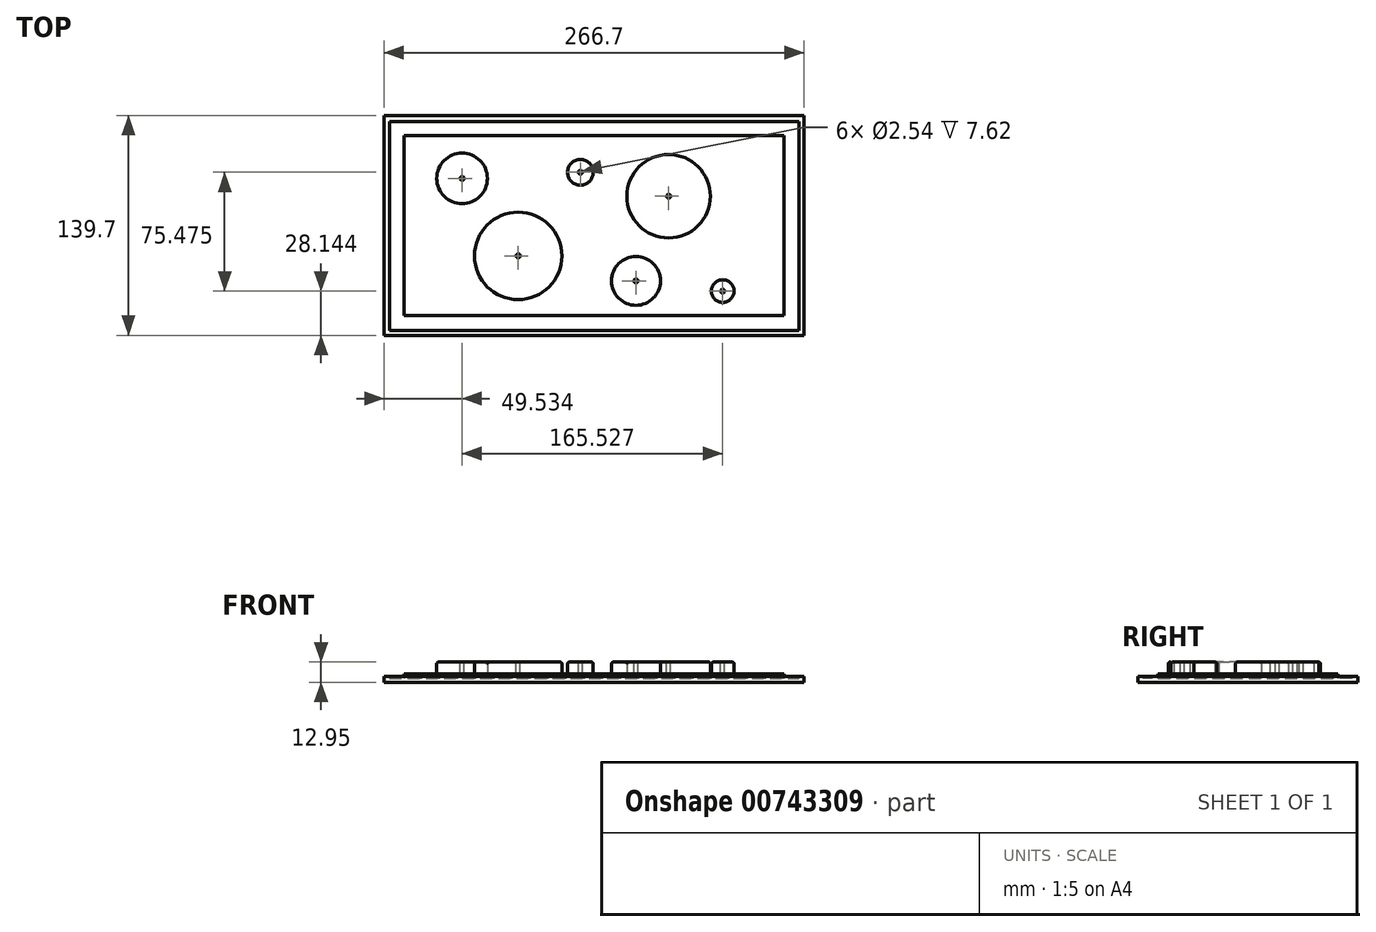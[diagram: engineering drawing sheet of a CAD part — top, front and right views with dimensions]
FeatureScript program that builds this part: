
annotation { "Feature Type Name" : "Feature", "Feature Type Description" : "" }
export const myFeature = defineFeature(function(context is Context, id is Id, definition is map)
    precondition{}
    {
        {
            var Q0;
            Q0=qCreatedBy(makeId("Top.planeOp"),FACE);
            var sketch = newSketch(context, id + "F0", { "sketchPlane" : qUnion([Q0])});
            skLineSegment(sketch, "E0.bottom", {"start": v(-127, 63.5) * mm, "end": v(127, 63.5) * mm});
            skLineSegment(sketch, "E0.top", {"start": v(-127, -63.5) * mm, "end": v(127, -63.5) * mm});
            skLineSegment(sketch, "E0.left", {"start": v(-127, 63.5) * mm, "end": v(-127, -63.5) * mm});
            skLineSegment(sketch, "E0.right", {"start": v(127, 63.5) * mm, "end": v(127, -63.5) * mm});
            skPoint(sketch, "E0.middle", {"position": v(0, 0) * mm});
            skSolve(sketch);
        }
        {
            var Q0;
            Q0 = qSketchRegion(id + "F0", true);
            extrude(context, id + "F1", {"entities" : qUnion([Q0]), "depth" : 0.25 * mm, "offsetDistance" : 25.4 * mm});
        }
        {
            var Q0;
            Q0=makeQuery(id+"F1.opExtrude","CAP_FACE",FACE,{"disambiguationData":[OSD([sQuery(id+"F0.wireOp",EDGE,"E0.bottom"),sQuery(id+"F0.wireOp",EDGE,"E0.top"),sQuery(id+"F0.wireOp",EDGE,"E0.left"),sQuery(id+"F0.wireOp",EDGE,"E0.right")])],"isStart":false});
            var sketch = newSketch(context, id + "F2", { "sketchPlane" : qUnion([Q0])});
            skLineSegment(sketch, "E1.bottom", {"start": v(-120.65, 57.15) * mm, "end": v(120.65, 57.15) * mm});
            skLineSegment(sketch, "E1.top", {"start": v(-120.65, -57.15) * mm, "end": v(120.65, -57.15) * mm});
            skLineSegment(sketch, "E1.left", {"start": v(-120.65, 57.15) * mm, "end": v(-120.65, -57.15) * mm});
            skLineSegment(sketch, "E1.right", {"start": v(120.65, 57.15) * mm, "end": v(120.65, -57.15) * mm});
            skPoint(sketch, "E1.middle", {"position": v(0, 0) * mm});
            skSolve(sketch);
        }
        {
            var Q0;
            Q0=makeQuery(id+"F1.opExtrude","CAP_FACE",FACE,{"disambiguationData":[OSD([sQuery(id+"F0.wireOp",EDGE,"E0.bottom"),sQuery(id+"F0.wireOp",EDGE,"E0.top"),sQuery(id+"F0.wireOp",EDGE,"E0.left"),sQuery(id+"F0.wireOp",EDGE,"E0.right")])],"isStart":false});
            var sketch = newSketch(context, id + "F3", { "sketchPlane" : qUnion([Q0])});
            skCircle(sketch, "E2", {"center": v(-83.82, 29.88) * mm, "radius": 16.08 * mm});
            skCircle(sketch, "E3", {"center": v(47.37, 18.54) * mm, "radius": 26.51 * mm});
            skCircle(sketch, "E4", {"center": v(26.64, -35.23) * mm, "radius": 15.5 * mm});
            skCircle(sketch, "E5", {"center": v(-48.18, -19.35) * mm, "radius": 27.8 * mm});
            skCircle(sketch, "E6", {"center": v(-8.67, 33.77) * mm, "radius": 8.16 * mm});
            skCircle(sketch, "E7", {"center": v(81.71, -41.7) * mm, "radius": 7.2 * mm});
            skSolve(sketch);
        }
        {
            var Q0;
            Q0 = qSketchRegion(id + "F3", true);
            extrude(context, id + "F4", {"entities" : qUnion([Q0]), "operationType" : NewBodyOperationType.ADD, "depth" : 12.7 * mm, "offsetDistance" : 25.4 * mm});
        }
        {
            var Q0;
            Q0=makeQuery(id+"F4.opExtrude","CAP_FACE",FACE,{"disambiguationData":[OSD([sQuery(id+"F3.wireOp",EDGE,"E2")])],"isStart":false});
            var sketch = newSketch(context, id + "F5", { "sketchPlane" : qUnion([Q0])});
            skCircle(sketch, "E8", {"center": v(-83.82, 29.88) * mm, "radius": 1.27 * mm});
            skSolve(sketch);
        }
        {
            var Q0;
            Q0=sQuery(id+"F5.wireOp",VERTEX,"E8.center");
            var Q1;
            Q1=makeQuery(id+"F1.opExtrude","SWEPT_BODY",BODY,{"disambiguationData":[OSD([sQuery(id+"F0.wireOp",EDGE,"E0.bottom"),sQuery(id+"F0.wireOp",EDGE,"E0.top"),sQuery(id+"F0.wireOp",EDGE,"E0.left"),sQuery(id+"F0.wireOp",EDGE,"E0.right")])]});
            hole(context, id + "F6", {"style" : HoleStyle.SIMPLE, "endStyle" : HoleEndStyle.THROUGH, "holeDiameter" : 2.54 * mm, "majorDiameter" : 6.35 * mm, "isTappedThrough" : true, "tappedDepth" : 12.7 * mm, "tapClearance" : 3, "locations" : qUnion([Q0]), "scope" : qUnion([Q1])});
        }
        {
            var Q0;
            Q0=makeQuery(id+"F4.opExtrude","CAP_FACE",FACE,{"disambiguationData":[OSD([sQuery(id+"F3.wireOp",EDGE,"E5")])],"isStart":false});
            var sketch = newSketch(context, id + "F7", { "sketchPlane" : qUnion([Q0])});
            skCircle(sketch, "E9", {"center": v(-48.18, -19.35) * mm, "radius": 1.27 * mm});
            skSolve(sketch);
        }
        {
            var Q0;
            Q0=sQuery(id+"F7.wireOp",VERTEX,"E9.center");
            var Q1;
            Q1=makeQuery(id+"F1.opExtrude","SWEPT_BODY",BODY,{"disambiguationData":[OSD([sQuery(id+"F0.wireOp",EDGE,"E0.bottom"),sQuery(id+"F0.wireOp",EDGE,"E0.top"),sQuery(id+"F0.wireOp",EDGE,"E0.left"),sQuery(id+"F0.wireOp",EDGE,"E0.right")])]});
            hole(context, id + "F8", {"style" : HoleStyle.SIMPLE, "endStyle" : HoleEndStyle.THROUGH, "holeDiameter" : 2.54 * mm, "majorDiameter" : 6.35 * mm, "isTappedThrough" : true, "tappedDepth" : 12.7 * mm, "tapClearance" : 3, "locations" : qUnion([Q0]), "scope" : qUnion([Q1])});
        }
        {
            var Q0;
            Q0=makeQuery(id+"F4.opExtrude","CAP_FACE",FACE,{"disambiguationData":[OSD([sQuery(id+"F3.wireOp",EDGE,"E6")])],"isStart":false});
            var sketch = newSketch(context, id + "F9", { "sketchPlane" : qUnion([Q0])});
            skCircle(sketch, "E10", {"center": v(-8.67, 33.77) * mm, "radius": 1.27 * mm});
            skSolve(sketch);
        }
        {
            var Q0;
            Q0=sQuery(id+"F9.wireOp",VERTEX,"E10.center");
            var Q1;
            Q1=makeQuery(id+"F1.opExtrude","SWEPT_BODY",BODY,{"disambiguationData":[OSD([sQuery(id+"F0.wireOp",EDGE,"E0.bottom"),sQuery(id+"F0.wireOp",EDGE,"E0.top"),sQuery(id+"F0.wireOp",EDGE,"E0.left"),sQuery(id+"F0.wireOp",EDGE,"E0.right")])]});
            hole(context, id + "F10", {"style" : HoleStyle.SIMPLE, "endStyle" : HoleEndStyle.THROUGH, "holeDiameter" : 2.54 * mm, "majorDiameter" : 6.35 * mm, "isTappedThrough" : true, "tappedDepth" : 12.7 * mm, "tapClearance" : 3, "locations" : qUnion([Q0]), "scope" : qUnion([Q1])});
        }
        {
            var Q0;
            Q0=makeQuery(id+"F4.opExtrude","CAP_EDGE",EDGE,{"disambiguationData":[OSD([sQuery(id+"F3.wireOp",EDGE,"E2")])],"isStart":false});
            fillet(context, id + "F11", {"entities" : qUnion([Q0]), "radius" : 1.27 * mm, "tangentPropagation" : true, "allowEdgeOverflow" : false});
        }
        {
            var Q0;
            Q0=makeQuery(id+"F4.opExtrude","CAP_EDGE",EDGE,{"disambiguationData":[OSD([sQuery(id+"F3.wireOp",EDGE,"E5")])],"isStart":false});
            fillet(context, id + "F12", {"entities" : qUnion([Q0]), "radius" : 1.27 * mm, "tangentPropagation" : true, "allowEdgeOverflow" : false});
        }
        {
            var Q0;
            Q0=makeQuery(id+"F4.opExtrude","CAP_EDGE",EDGE,{"disambiguationData":[OSD([sQuery(id+"F3.wireOp",EDGE,"E6")])],"isStart":false});
            fillet(context, id + "F13", {"entities" : qUnion([Q0]), "radius" : 1.27 * mm, "tangentPropagation" : true, "allowEdgeOverflow" : false});
        }
        {
            var Q0;
            Q0=makeQuery(id+"F4.opExtrude","CAP_EDGE",EDGE,{"disambiguationData":[OSD([sQuery(id+"F3.wireOp",EDGE,"E3")])],"isStart":false});
            fillet(context, id + "F14", {"entities" : qUnion([Q0]), "radius" : 1.27 * mm, "tangentPropagation" : true, "allowEdgeOverflow" : false});
        }
        {
            var Q0;
            Q0=makeQuery(id+"F4.opExtrude","CAP_EDGE",EDGE,{"disambiguationData":[OSD([sQuery(id+"F3.wireOp",EDGE,"E4")])],"isStart":false});
            fillet(context, id + "F15", {"entities" : qUnion([Q0]), "radius" : 1.27 * mm, "tangentPropagation" : true, "allowEdgeOverflow" : false});
        }
        {
            var Q0;
            Q0=makeQuery(id+"F4.opExtrude","CAP_EDGE",EDGE,{"disambiguationData":[OSD([sQuery(id+"F3.wireOp",EDGE,"E7")])],"isStart":false});
            fillet(context, id + "F16", {"entities" : qUnion([Q0]), "radius" : 1.27 * mm, "tangentPropagation" : true, "allowEdgeOverflow" : false});
        }
        {
            var Q0;
            Q0=makeQuery(id+"F4.opExtrude","CAP_FACE",FACE,{"disambiguationData":[OSD([sQuery(id+"F3.wireOp",EDGE,"E3")])],"isStart":false});
            var sketch = newSketch(context, id + "F17", { "sketchPlane" : qUnion([Q0])});
            skCircle(sketch, "E11", {"center": v(47.37, 18.54) * mm, "radius": 1.27 * mm});
            skSolve(sketch);
        }
        {
            var Q0;
            Q0=sQuery(id+"F17.wireOp",VERTEX,"E11.center");
            var Q1;
            Q1=makeQuery(id+"F1.opExtrude","SWEPT_BODY",BODY,{"disambiguationData":[OSD([sQuery(id+"F0.wireOp",EDGE,"E0.bottom"),sQuery(id+"F0.wireOp",EDGE,"E0.top"),sQuery(id+"F0.wireOp",EDGE,"E0.left"),sQuery(id+"F0.wireOp",EDGE,"E0.right")])]});
            hole(context, id + "F18", {"style" : HoleStyle.SIMPLE, "endStyle" : HoleEndStyle.THROUGH, "holeDiameter" : 2.54 * mm, "majorDiameter" : 6.35 * mm, "isTappedThrough" : true, "tappedDepth" : 12.7 * mm, "tapClearance" : 3, "locations" : qUnion([Q0]), "scope" : qUnion([Q1])});
        }
        {
            var Q0;
            Q0=makeQuery(id+"F4.opExtrude","CAP_FACE",FACE,{"disambiguationData":[OSD([sQuery(id+"F3.wireOp",EDGE,"E4")])],"isStart":false});
            var sketch = newSketch(context, id + "F19", { "sketchPlane" : qUnion([Q0])});
            skCircle(sketch, "E12", {"center": v(26.64, -35.23) * mm, "radius": 1.27 * mm});
            skSolve(sketch);
        }
        {
            var Q0;
            Q0=sQuery(id+"F19.wireOp",VERTEX,"E12.center");
            var Q1;
            Q1=makeQuery(id+"F1.opExtrude","SWEPT_BODY",BODY,{"disambiguationData":[OSD([sQuery(id+"F0.wireOp",EDGE,"E0.bottom"),sQuery(id+"F0.wireOp",EDGE,"E0.top"),sQuery(id+"F0.wireOp",EDGE,"E0.left"),sQuery(id+"F0.wireOp",EDGE,"E0.right")])]});
            hole(context, id + "F20", {"style" : HoleStyle.SIMPLE, "endStyle" : HoleEndStyle.THROUGH, "holeDiameter" : 2.54 * mm, "majorDiameter" : 6.35 * mm, "isTappedThrough" : true, "tappedDepth" : 12.7 * mm, "tapClearance" : 3, "locations" : qUnion([Q0]), "scope" : qUnion([Q1])});
        }
        {
            var Q0;
            Q0=makeQuery(id+"F4.opExtrude","CAP_FACE",FACE,{"disambiguationData":[OSD([sQuery(id+"F3.wireOp",EDGE,"E7")])],"isStart":false});
            var sketch = newSketch(context, id + "F21", { "sketchPlane" : qUnion([Q0])});
            skCircle(sketch, "E13", {"center": v(81.71, -41.7) * mm, "radius": 1.27 * mm});
            skSolve(sketch);
        }
        {
            var Q0;
            Q0=sQuery(id+"F21.wireOp",VERTEX,"E13.center");
            var Q1;
            Q1=makeQuery(id+"F1.opExtrude","SWEPT_BODY",BODY,{"disambiguationData":[OSD([sQuery(id+"F0.wireOp",EDGE,"E0.bottom"),sQuery(id+"F0.wireOp",EDGE,"E0.top"),sQuery(id+"F0.wireOp",EDGE,"E0.left"),sQuery(id+"F0.wireOp",EDGE,"E0.right")])]});
            hole(context, id + "F22", {"style" : HoleStyle.SIMPLE, "endStyle" : HoleEndStyle.THROUGH, "holeDiameter" : 2.54 * mm, "majorDiameter" : 6.35 * mm, "isTappedThrough" : true, "tappedDepth" : 12.7 * mm, "tapClearance" : 3, "locations" : qUnion([Q0]), "scope" : qUnion([Q1])});
        }
        {
            var Q0;
            Q0=qCreatedBy(makeId("Top.planeOp"),FACE);
            var sketch = newSketch(context, id + "F23", { "sketchPlane" : qUnion([Q0])});
            skLineSegment(sketch, "E14.bottom", {"start": v(133.35, 69.85) * mm, "end": v(-133.35, 69.85) * mm});
            skLineSegment(sketch, "E14.top", {"start": v(133.35, -69.85) * mm, "end": v(-133.35, -69.85) * mm});
            skLineSegment(sketch, "E14.left", {"start": v(133.35, 69.85) * mm, "end": v(133.35, -69.85) * mm});
            skLineSegment(sketch, "E14.right", {"start": v(-133.35, 69.85) * mm, "end": v(-133.35, -69.85) * mm});
            skPoint(sketch, "E14.middle", {"position": v(0, 0) * mm});
            skSolve(sketch);
        }
        {
            var Q0;
            Q0 = qSketchRegion(id + "F23", true);
            extrude(context, id + "F24", {"entities" : qUnion([Q0]), "operationType" : NewBodyOperationType.ADD, "depth" : 2.54 * mm, "offsetDistance" : 25.4 * mm});
        }
        {
            var Q0;
            Q0 = qSketchRegion(id + "F2", true);
            extrude(context, id + "F25", {"entities" : qUnion([Q0]), "operationType" : NewBodyOperationType.ADD, "depth" : 5.08 * mm, "offsetDistance" : 25.4 * mm});
        }
        {
            var Q0;
            {var subQ0=sQuery(id+"F23.wireOp",EDGE,"E14.left");var subQ1=sQuery(id+"F23.wireOp",EDGE,"E14.right");var subQ2=sQuery(id+"F23.wireOp",EDGE,"E14.bottom");var subQ3=sQuery(id+"F23.wireOp",EDGE,"E14.top");Q0=makeQuery(id+"F24.boolean.opBoolean","SPLIT",FACE,{"disambiguationData":[TD([makeQuery(id+"F4.opExtrude","SWEPT_FACE",FACE,{"disambiguationData":[OSD([sQuery(id+"F3.wireOp",EDGE,"E2")])]})])],"derivedFrom":makeQuery(id+"F24.opExtrude","CAP_FACE",FACE,{"disambiguationData":[OSD([subQ2,subQ3,subQ0,subQ1])],"isStart":false})});}
            var sketch = newSketch(context, id + "F26", { "sketchPlane" : qUnion([Q0])});
            skLineSegment(sketch, "E15.bottom", {"start": v(-129.81, 65.84) * mm, "end": v(130.3, 65.84) * mm});
            skLineSegment(sketch, "E15.top", {"start": v(-129.81, -66.65) * mm, "end": v(130.3, -66.65) * mm});
            skLineSegment(sketch, "E15.left", {"start": v(-129.81, 65.84) * mm, "end": v(-129.81, -66.65) * mm});
            skLineSegment(sketch, "E15.right", {"start": v(130.3, 65.84) * mm, "end": v(130.3, -66.65) * mm});
            skLineSegment(sketch, "E16.bottom", {"start": v(-133.35, 69.85) * mm, "end": v(133.35, 69.85) * mm});
            skLineSegment(sketch, "E16.top", {"start": v(-133.35, -69.85) * mm, "end": v(133.35, -69.85) * mm});
            skLineSegment(sketch, "E16.left", {"start": v(-133.35, 69.85) * mm, "end": v(-133.35, -69.85) * mm});
            skLineSegment(sketch, "E16.right", {"start": v(133.35, 69.85) * mm, "end": v(133.35, -69.85) * mm});
            skSolve(sketch);
        }
        {
            var Q0;
            Q0=makeQuery(id+"F26.imprint","IMPRINT",FACE,{"disambiguationData":[TD([[makeQuery(id+"F26.imprint","IMPRINT",EDGE,{"derivedFrom":sQuery(id+"F26.wireOp",EDGE,"E15.bottom")}),1.0]])]});
            extrude(context, id + "F27", {"entities" : qUnion([Q0]), "operationType" : NewBodyOperationType.ADD, "depth" : 1.27 * mm, "offsetDistance" : 25.4 * mm});
        }
    });
